# Revit family: Sanitary_Accessories_57104-PRESTO-Linea-Wall-mounted-sensor-mixer-FR
name_source: partatom
category: Pipe Accessories
revit_build: Autodesk Revit 2018 (Build: 20190510_1515(x64)
units: mm (PartAtom-declared; Revit-internal decimal feet)

## family parameters
Always vertical = Yes
Cut with Voids When Loaded = No
Part Type = Normal
Round Connector Dimension = Use Diameter
Shared = No
Work Plane-Based = No

## types (1)
- 57104 PRESTO Linea  - Mitigeur électronique mural pour lavabo
    Adresse = 7, RUE RACINE - 92542 MONTROUGE CEDEX FRANCE
    BIMobject category = Sanitary Accessories
    Description = Traversée de cloison, 230V, 3l/min
Déclenchement sans contact adapté PMR
    Diamètre Nominal = 10 mm  [stored 0.0328084 ft]
    Edition number = 1
    Flux = 3 L/min
    Fonction = Débit : 3 l/mn par régulateur de débit intégré
Aérateur anti-tartre haute qualité
    Garantie = 10 ans
    Hauteur = 60 mm  [stored 0.19685 ft]
    Installation instructions = http://www.prestodatashare.com
    Largeur = 60 mm  [stored 0.19685 ft]
    Lien CCTP = http://www.prestodatashare.com
    Lien fiche produit = http://www.prestodatashare.com
    Lien notice d'utilisation = http://www.prestodatashare.com
    Manufacturer = LES ROBINETS PRESTO S.A.
    Manufacturer name = Presto
    Model = 57104
    Product Guid = 9273f4c4-bf84-45c7-b78e-0bd91acdbc88
    Product SKU = PRE-LINEA-57104
    Product data url = https://www.bimobject.com
    Product family = Sanitary
    Product group = Washbasin
    Product name = 57104 PRESTO Linea - Wall-mounted sensor mixer
    Product url = http://www.prestodatashare.com
    Profondeur = 258 mm
    QR code = https://www.bimobject.com
    Raccordement = Alimentation hydraulique : Flexibles G 3/8'' (12x17)
Alimentation électrique : Avec transformateur 230 V AC / 7 V DC dans boîtier étanche IP65
    Technical description = http://www.prestodatashare.com
    URL = http://www.presto.fr
    URL du produit = http://www.prestodatashare.com

note: [stored X ft] marks values corroborated as IEEE doubles in the binary element streams (Revit-internal decimal feet)

## geometry (parser evidence)
native form markers: Sweep x3
no freeform markers — native parametric forms only
